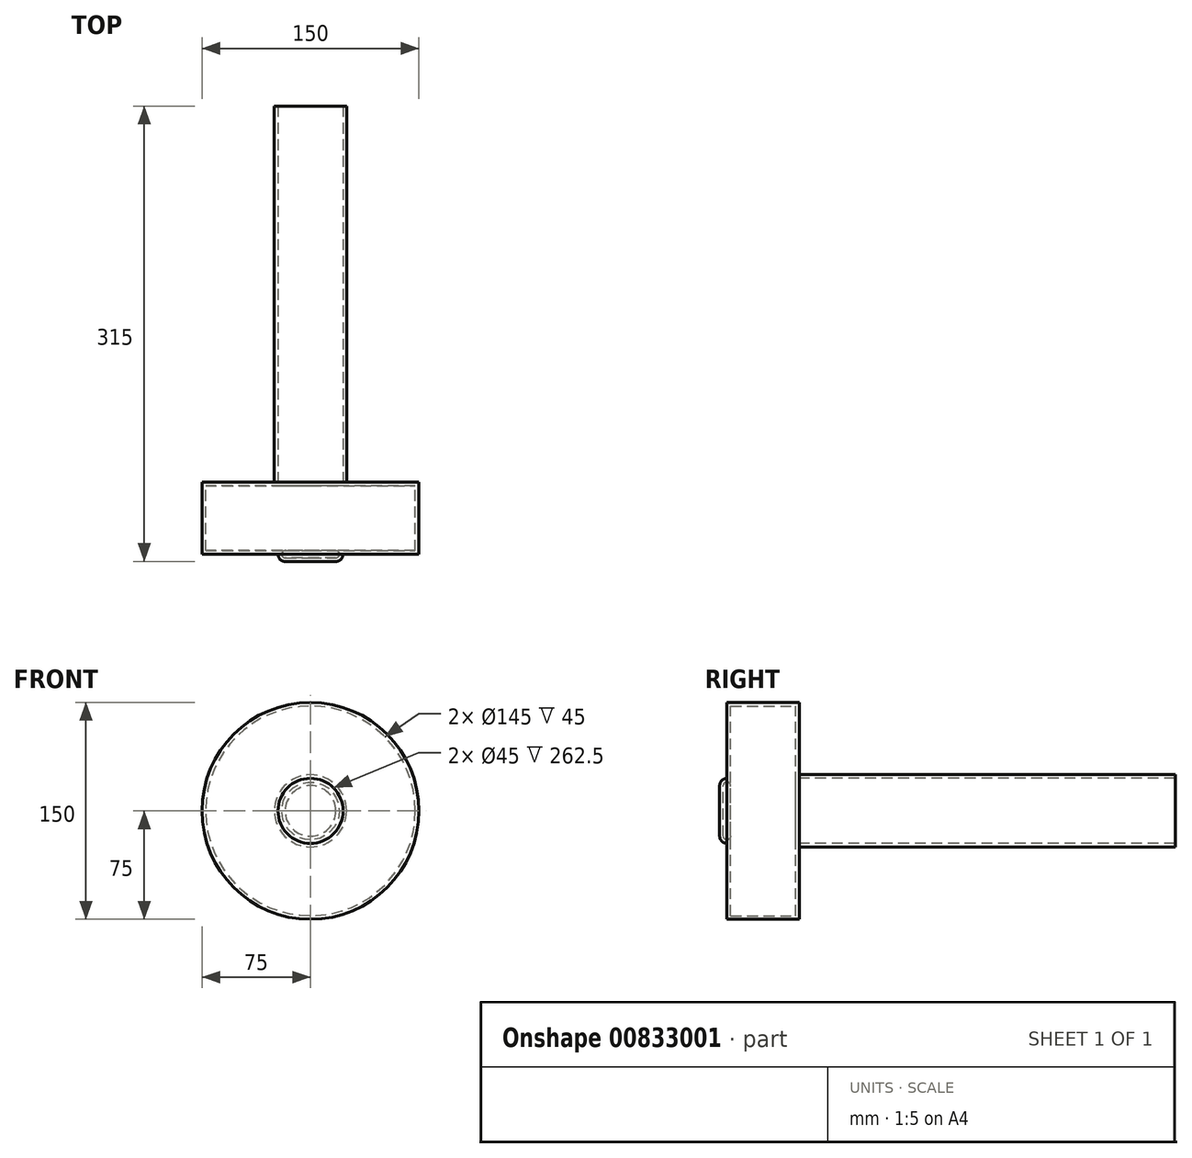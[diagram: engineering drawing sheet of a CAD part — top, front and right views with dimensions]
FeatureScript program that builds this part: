
annotation { "Feature Type Name" : "Feature", "Feature Type Description" : "" }
export const myFeature = defineFeature(function(context is Context, id is Id, definition is map)
    precondition{}
    {
        {
            var Q0;
            Q0=qCreatedBy(makeId("Front.planeOp"),FACE);
            var sketch = newSketch(context, id + "F0", { "sketchPlane" : qUnion([Q0])});
            skCircle(sketch, "E0", {"center": v(0, 0) * mm, "radius": 75 * mm});
            skSolve(sketch);
        }
        {
            var Q0;
            Q0 = qSketchRegion(id + "F0", true);
            extrude(context, id + "F1", {"entities" : qUnion([Q0]), "depth" : 50 * mm, "offsetDistance" : 25 * mm});
        }
        {
            var Q0;
            Q0=qCreatedBy(makeId("Front.planeOp"),FACE);
            var sketch = newSketch(context, id + "F2", { "sketchPlane" : qUnion([Q0])});
            skCircle(sketch, "E1", {"center": v(0, 0) * mm, "radius": 25 * mm});
            skSolve(sketch);
        }
        {
            var Q0;
            Q0 = qSketchRegion(id + "F2", true);
            extrude(context, id + "F3", {"entities" : qUnion([Q0]), "operationType" : NewBodyOperationType.ADD, "oppositeDirection" : true, "depth" : 260 * mm, "offsetDistance" : 25 * mm});
        }
        {
            var Q0;
            Q0=makeQuery(id+"F1.opExtrude","CAP_FACE",FACE,{"disambiguationData":[OSD([sQuery(id+"F0.wireOp",EDGE,"E0")])],"isStart":false});
            var sketch = newSketch(context, id + "F4", { "sketchPlane" : qUnion([Q0])});
            skCircle(sketch, "E2", {"center": v(0, 0) * mm, "radius": 22.5 * mm});
            skSolve(sketch);
        }
        {
            var Q0;
            Q0=makeQuery(id+"F4.imprint","IMPRINT",FACE,{"disambiguationData":[TD([[makeQuery(id+"F4.imprint","IMPRINT",EDGE,{"derivedFrom":sQuery(id+"F4.wireOp",EDGE,"E2")}),1.0]])]});
            extrude(context, id + "F5", {"entities" : qUnion([Q0]), "operationType" : NewBodyOperationType.ADD, "depth" : 5 * mm, "offsetDistance" : 25 * mm});
        }
        {
            var Q0;
            Q0=makeQuery(id+"F5.opExtrude","CAP_EDGE",EDGE,{"disambiguationData":[OSD([sQuery(id+"F4.wireOp",EDGE,"E2")])],"isStart":false});
            fillet(context, id + "F6", {"entities" : qUnion([Q0]), "radius" : 5 * mm, "tangentPropagation" : true, "allowEdgeOverflow" : false});
        }
        {
            var Q0;
            Q0=makeQuery(id+"F3.opExtrude","CAP_FACE",FACE,{"disambiguationData":[OSD([sQuery(id+"F2.wireOp",EDGE,"E1")])],"isStart":false});
            shell(context, id + "F7", {"entities" : qUnion([Q0]), "thickness" : 2.5 * mm});
        }
        {
            var Q0;
            Q0=makeQuery(id+"F1.opExtrude","SWEPT_BODY",BODY,{"disambiguationData":[OSD([sQuery(id+"F0.wireOp",EDGE,"E0")])]});
            transform(context, id + "F8", {"entities" : qUnion([Q0]), "transformType" : TransformType.TRANSLATION_3D, "dx" : 0 * mm, "dy" : 0 * mm, "dz" : 0 * mm, "makeCopy" : true});
        }
    });
